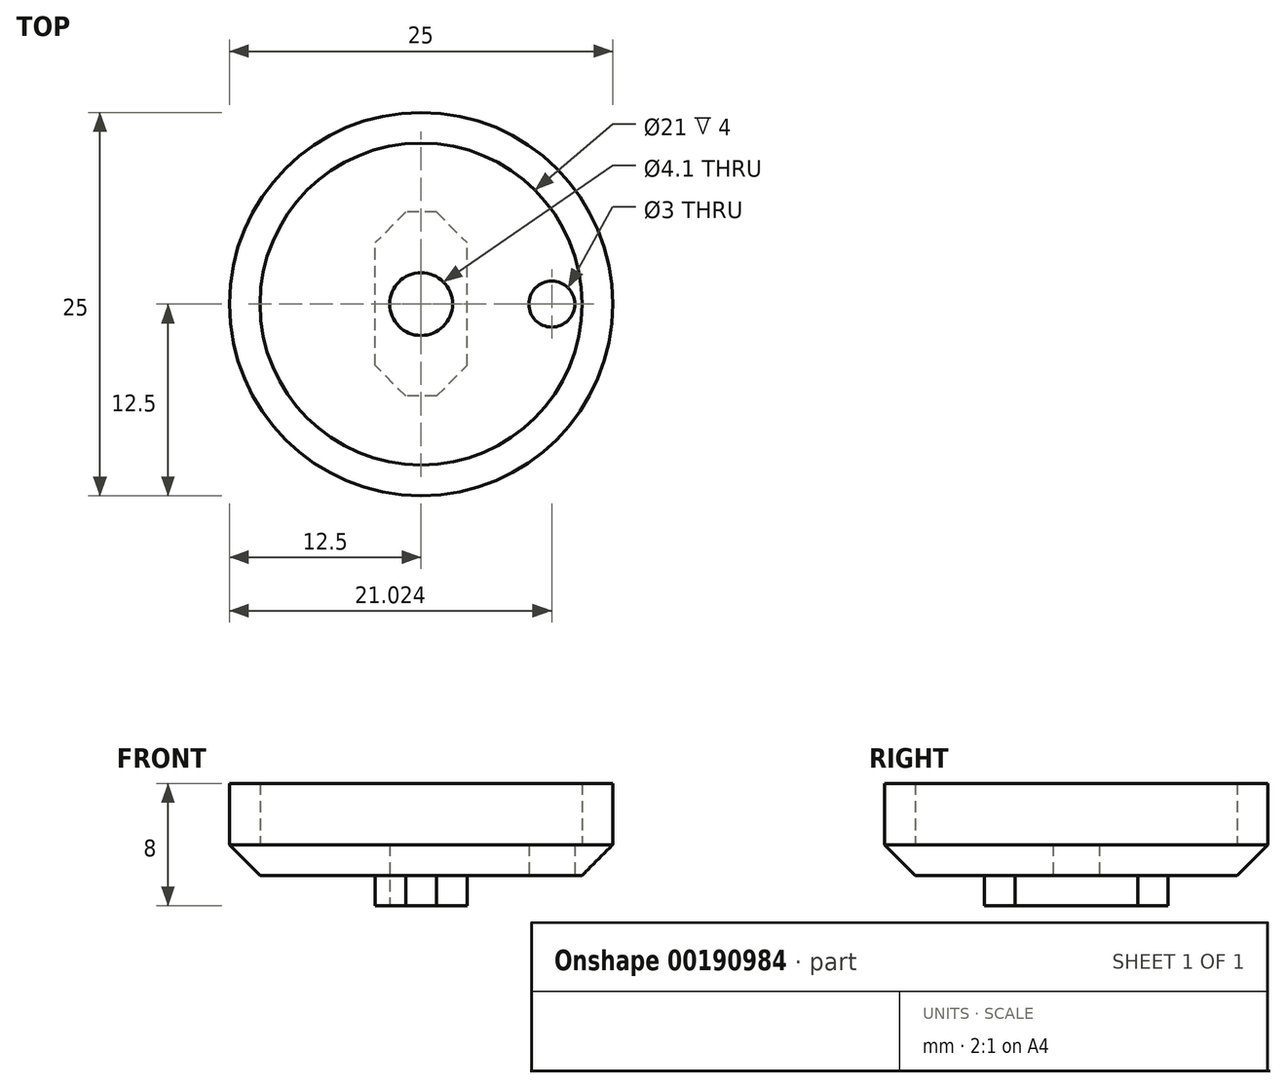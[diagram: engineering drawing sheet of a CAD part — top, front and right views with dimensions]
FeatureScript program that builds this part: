
annotation { "Feature Type Name" : "Feature", "Feature Type Description" : "" }
export const myFeature = defineFeature(function(context is Context, id is Id, definition is map)
    precondition{}
    {
        {
            var Q0;
            Q0=qCreatedBy(makeId("Top.planeOp"),FACE);
            var sketch = newSketch(context, id + "F0", { "sketchPlane" : qUnion([Q0])});
            skCircle(sketch, "E0", {"center": v(0, 0) * mm, "radius": 12.5 * mm});
            skSolve(sketch);
        }
        {
            var Q0;
            Q0 = qSketchRegion(id + "F0", true);
            extrude(context, id + "F1", {"entities" : qUnion([Q0]), "depth" : 6 * mm});
        }
        {
            var Q0;
            Q0=makeQuery(id+"F1.opExtrude","CAP_FACE",FACE,{"disambiguationData":[OSD([sQuery(id+"F0.wireOp",EDGE,"E0")])],"isStart":false});
            shell(context, id + "F2", {"entities" : qUnion([Q0]), "thickness" : 2 * mm});
        }
        {
            var Q0;
            Q0=makeQuery(id+"F1.opExtrude","CAP_EDGE",EDGE,{"disambiguationData":[OSD([sQuery(id+"F0.wireOp",EDGE,"E0")])],"isStart":true});
            chamfer(context, id + "F3", {"entities" : qUnion([Q0]), "width" : 2 * mm, "tangentPropagation" : true});
        }
        {
            var Q0;
            Q0=makeQuery(id+"F1.opExtrude","CAP_FACE",FACE,{"disambiguationData":[OSD([sQuery(id+"F0.wireOp",EDGE,"E0")])],"isStart":true});
            var sketch = newSketch(context, id + "F4", { "sketchPlane" : qUnion([Q0])});
            skLineSegment(sketch, "E1.bottom", {"start": v(3, 6) * mm, "end": v(-3, 6) * mm});
            skLineSegment(sketch, "E1.top", {"start": v(3, -6) * mm, "end": v(-3, -6) * mm});
            skLineSegment(sketch, "E1.left", {"start": v(3, 6) * mm, "end": v(3, -6) * mm});
            skLineSegment(sketch, "E1.right", {"start": v(-3, 6) * mm, "end": v(-3, -6) * mm});
            skSolve(sketch);
        }
        {
            var Q0;
            Q0=makeQuery(id+"F4.imprint","IMPRINT",FACE,{"disambiguationData":[TD([[makeQuery(id+"F4.imprint","IMPRINT",EDGE,{"derivedFrom":sQuery(id+"F4.wireOp",EDGE,"E1.bottom")}),1.0]])]});
            extrude(context, id + "F5", {"entities" : qUnion([Q0]), "operationType" : NewBodyOperationType.ADD, "depth" : 2 * mm});
        }
        {
            var Q0;
            Q0=makeQuery(id+"F5.opExtrude","SWEPT_EDGE",EDGE,{"disambiguationData":[OSD([sQuery(id+"F4.wireOp",EDGE,"E1.bottom"),sQuery(id+"F4.wireOp",EDGE,"E1.left")])]});
            var Q1;
            Q1=makeQuery(id+"F5.opExtrude","SWEPT_EDGE",EDGE,{"disambiguationData":[OSD([sQuery(id+"F4.wireOp",EDGE,"E1.bottom"),sQuery(id+"F4.wireOp",EDGE,"E1.right")])]});
            var Q2;
            Q2=makeQuery(id+"F5.opExtrude","SWEPT_EDGE",EDGE,{"disambiguationData":[OSD([sQuery(id+"F4.wireOp",EDGE,"E1.top"),sQuery(id+"F4.wireOp",EDGE,"E1.left")])]});
            var Q3;
            Q3=makeQuery(id+"F5.opExtrude","SWEPT_EDGE",EDGE,{"disambiguationData":[OSD([sQuery(id+"F4.wireOp",EDGE,"E1.top"),sQuery(id+"F4.wireOp",EDGE,"E1.right")])]});
            chamfer(context, id + "F6", {"entities" : qUnion([Q0, Q1, Q2, Q3]), "width" : 2 * mm, "tangentPropagation" : true});
        }
        {
            var Q0;
            Q0=makeQuery(id+"F5.opExtrude","CAP_FACE",FACE,{"disambiguationData":[OSD([sQuery(id+"F4.wireOp",EDGE,"E1.bottom"),sQuery(id+"F4.wireOp",EDGE,"E1.top"),sQuery(id+"F4.wireOp",EDGE,"E1.left"),sQuery(id+"F4.wireOp",EDGE,"E1.right")])],"isStart":false});
            var sketch = newSketch(context, id + "F7", { "sketchPlane" : qUnion([Q0])});
            skCircle(sketch, "E2", {"center": v(0, 0) * mm, "radius": 2.05 * mm});
            skSolve(sketch);
        }
        {
            var Q0;
            Q0=makeQuery(id+"F7.imprint","IMPRINT",FACE,{"disambiguationData":[TD([[makeQuery(id+"F7.imprint","IMPRINT",EDGE,{"derivedFrom":sQuery(id+"F7.wireOp",EDGE,"E2")}),1.0]])]});
            extrude(context, id + "F8", {"entities" : qUnion([Q0]), "operationType" : NewBodyOperationType.REMOVE, "oppositeDirection" : true, "depth" : 25 * mm});
        }
        {
            var Q0;
            Q0=makeQuery(id+"F1.opExtrude","CAP_FACE",FACE,{"disambiguationData":[OSD([sQuery(id+"F0.wireOp",EDGE,"E0")])],"isStart":true});
            var sketch = newSketch(context, id + "F9", { "sketchPlane" : qUnion([Q0])});
            skCircle(sketch, "E3", {"center": v(8.52, 0) * mm, "radius": 1.5 * mm});
            skSolve(sketch);
        }
        {
            var Q0;
            Q0=makeQuery(id+"F9.imprint","IMPRINT",FACE,{"disambiguationData":[TD([[makeQuery(id+"F9.imprint","IMPRINT",EDGE,{"derivedFrom":sQuery(id+"F9.wireOp",EDGE,"E3")}),1.0]])]});
            extrude(context, id + "F10", {"entities" : qUnion([Q0]), "operationType" : NewBodyOperationType.REMOVE, "oppositeDirection" : true, "depth" : 25 * mm});
        }
    });
